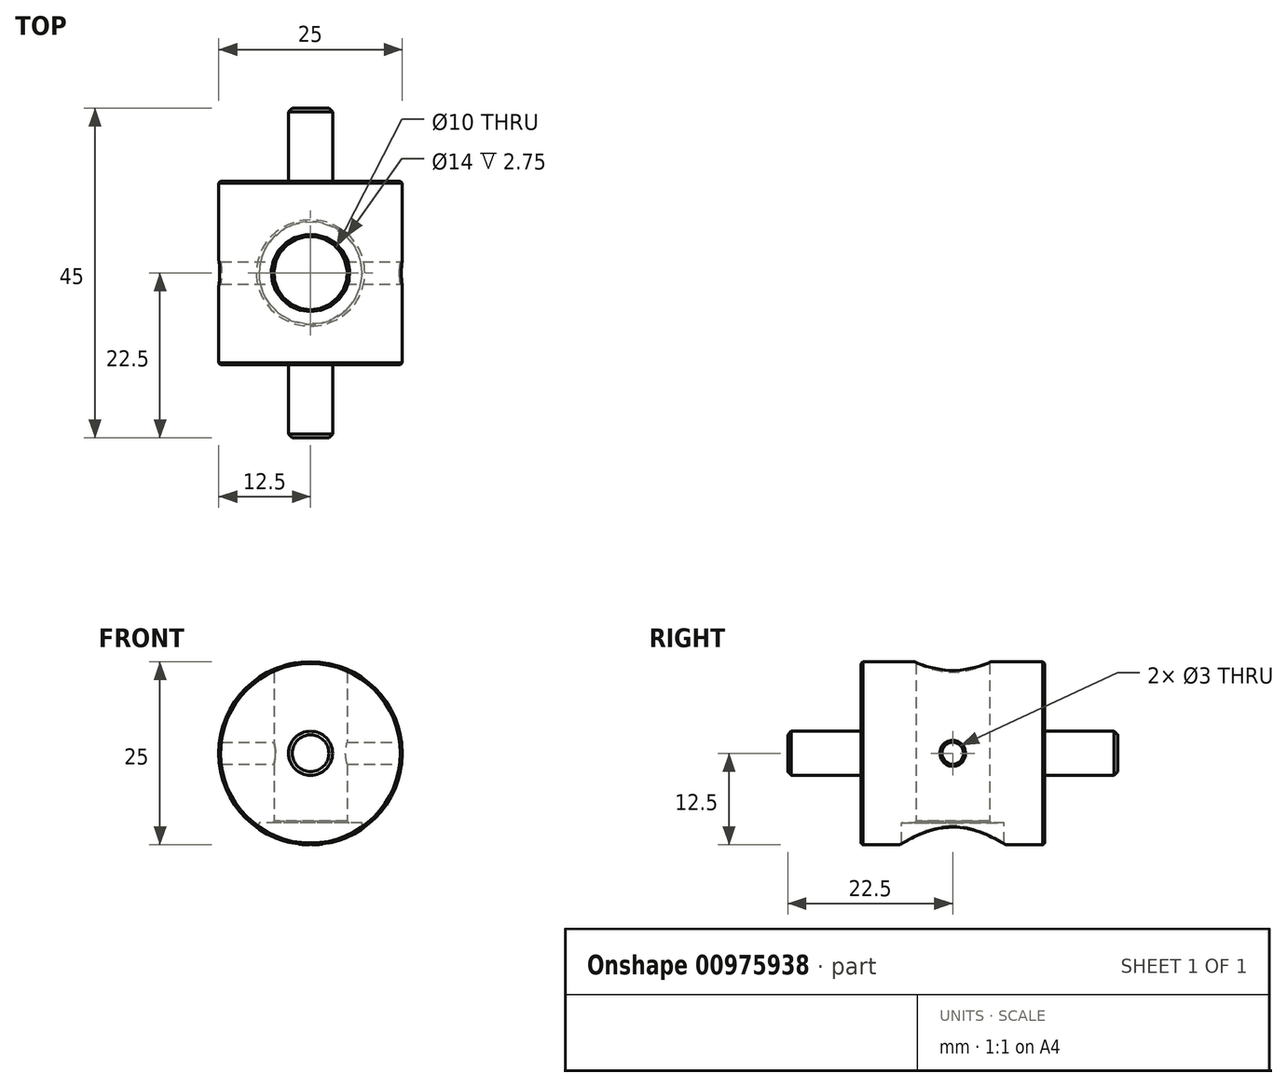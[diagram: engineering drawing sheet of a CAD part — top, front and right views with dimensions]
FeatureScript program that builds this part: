
annotation { "Feature Type Name" : "Feature", "Feature Type Description" : "" }
export const myFeature = defineFeature(function(context is Context, id is Id, definition is map)
    precondition{}
    {
        {
            var Q0;
            Q0=qCreatedBy(makeId("Front.planeOp"),FACE);
            var sketch = newSketch(context, id + "F0", { "sketchPlane" : qUnion([Q0])});
            skCircle(sketch, "E0", {"center": v(0, 0) * mm, "radius": 12.5 * mm});
            skSolve(sketch);
        }
        {
            var Q0;
            Q0=makeQuery(id+"F0.imprint","IMPRINT",FACE,{"disambiguationData":[TD([[makeQuery(id+"F0.imprint","IMPRINT",EDGE,{"derivedFrom":sQuery(id+"F0.wireOp",EDGE,"E0")}),1.0]])]});
            extrude(context, id + "F1", {"entities" : qUnion([Q0]), "depth" : 25 * mm, "offsetDistance" : 25 * mm, "symmetric" : true});
        }
        {
            var Q0;
            Q0=makeQuery(id+"F1.opExtrude","CAP_FACE",FACE,{"disambiguationData":[OSD([sQuery(id+"F0.wireOp",EDGE,"E0")])],"isStart":false});
            var sketch = newSketch(context, id + "F2", { "sketchPlane" : qUnion([Q0])});
            skCircle(sketch, "E1", {"center": v(0, 0) * mm, "radius": 3 * mm});
            skSolve(sketch);
        }
        {
            var Q0;
            Q0=makeQuery(id+"F2.imprint","IMPRINT",FACE,{"disambiguationData":[TD([[makeQuery(id+"F2.imprint","IMPRINT",EDGE,{"derivedFrom":sQuery(id+"F2.wireOp",EDGE,"E1")}),1.0]])]});
            extrude(context, id + "F3", {"entities" : qUnion([Q0]), "operationType" : NewBodyOperationType.ADD, "depth" : 10 * mm, "offsetDistance" : 25 * mm});
        }
        {
            var Q0;
            Q0=makeQuery(id+"F1.opExtrude","CAP_FACE",FACE,{"disambiguationData":[OSD([sQuery(id+"F0.wireOp",EDGE,"E0")])],"isStart":true});
            var sketch = newSketch(context, id + "F4", { "sketchPlane" : qUnion([Q0])});
            skCircle(sketch, "E2", {"center": v(0, 0) * mm, "radius": 3 * mm});
            skSolve(sketch);
        }
        {
            var Q0;
            Q0=makeQuery(id+"F4.imprint","IMPRINT",FACE,{"disambiguationData":[TD([[makeQuery(id+"F4.imprint","IMPRINT",EDGE,{"derivedFrom":sQuery(id+"F4.wireOp",EDGE,"E2")}),1.0]])]});
            extrude(context, id + "F5", {"entities" : qUnion([Q0]), "operationType" : NewBodyOperationType.ADD, "depth" : 10 * mm, "offsetDistance" : 25 * mm});
        }
        {
            var Q0;
            Q0=makeQuery(id+"F5.opExtrude","CAP_EDGE",EDGE,{"disambiguationData":[OSD([sQuery(id+"F4.wireOp",EDGE,"E2")])],"isStart":false});
            var Q1;
            Q1=makeQuery(id+"F3.opExtrude","CAP_EDGE",EDGE,{"disambiguationData":[OSD([sQuery(id+"F2.wireOp",EDGE,"E1")])],"isStart":false});
            chamfer(context, id + "F6", {"entities" : qUnion([Q0, Q1]), "width" : 0.5 * mm, "tangentPropagation" : true});
        }
        {
            var Q0;
            Q0=makeQuery(id+"F1.opExtrude","CAP_EDGE",EDGE,{"disambiguationData":[OSD([sQuery(id+"F0.wireOp",EDGE,"E0")])],"isStart":true});
            var Q1;
            Q1=makeQuery(id+"F1.opExtrude","CAP_EDGE",EDGE,{"disambiguationData":[OSD([sQuery(id+"F0.wireOp",EDGE,"E0")])],"isStart":false});
            chamfer(context, id + "F7", {"entities" : qUnion([Q0, Q1]), "width" : 0.25 * mm, "tangentPropagation" : true});
        }
        {
            var Q0;
            Q0=qCreatedBy(makeId("Top.planeOp"),FACE);
            var sketch = newSketch(context, id + "F8", { "sketchPlane" : qUnion([Q0])});
            skCircle(sketch, "E3", {"center": v(0, 0) * mm, "radius": 5 * mm});
            skSolve(sketch);
        }
        {
            var Q0;
            Q0 = qSketchRegion(id + "F8", true);
            extrude(context, id + "F9", {"entities" : qUnion([Q0]), "operationType" : NewBodyOperationType.REMOVE, "depth" : 25 * mm, "offsetDistance" : 25 * mm, "symmetric" : true});
        }
        {
            var Q0;
            Q0=qCreatedBy(makeId("Top.planeOp"),FACE);
            var sketch = newSketch(context, id + "F10", { "sketchPlane" : qUnion([Q0])});
            skCircle(sketch, "E4", {"center": v(0, 0) * mm, "radius": 7 * mm});
            skSolve(sketch);
        }
        {
            var Q0;
            Q0 = qSketchRegion(id + "F10", true);
            extrude(context, id + "F11", {"entities" : qUnion([Q0]), "operationType" : NewBodyOperationType.REMOVE, "oppositeDirection" : true, "depth" : 25 * mm, "offsetDistance" : 25 * mm, "hasSecondDirection" : true, "secondDirectionOppositeDirection" : true, "secondDirectionDepth" : 9.5 * mm});
        }
        {
            var Q0;
            Q0=qCreatedBy(makeId("Right.planeOp"),FACE);
            var sketch = newSketch(context, id + "F12", { "sketchPlane" : qUnion([Q0])});
            skCircle(sketch, "E5", {"center": v(0, 0) * mm, "radius": 1.5 * mm});
            skSolve(sketch);
        }
        {
            var Q0;
            Q0 = qSketchRegion(id + "F12", true);
            extrude(context, id + "F13", {"entities" : qUnion([Q0]), "operationType" : NewBodyOperationType.REMOVE, "oppositeDirection" : true, "depth" : 25 * mm, "offsetDistance" : 25 * mm, "symmetric" : true});
        }
        {
            var Q0;
            Q0=makeQuery(id+"F13.boolean.opBoolean","INTERSECT",EDGE,{"disambiguationData":[OD(1.0)],"derivedFrom":[makeQuery(id+"F1.opExtrude","SWEPT_FACE",FACE,{"disambiguationData":[OSD([sQuery(id+"F0.wireOp",EDGE,"E0")])]}),makeQuery(id+"F13.opExtrude","SWEPT_FACE",FACE,{"disambiguationData":[OSD([sQuery(id+"F12.wireOp",EDGE,"E5")])]})]});
            var Q1;
            Q1=makeQuery(id+"F11.boolean.opBoolean","INTERSECT",EDGE,{"derivedFrom":[makeQuery(id+"F1.opExtrude","SWEPT_FACE",FACE,{"disambiguationData":[OSD([sQuery(id+"F0.wireOp",EDGE,"E0")])]}),makeQuery(id+"F11.opExtrude","SWEPT_FACE",FACE,{"disambiguationData":[OSD([sQuery(id+"F10.wireOp",EDGE,"E4")])]})]});
            var Q2;
            Q2=makeQuery(id+"F9.boolean.opBoolean","INTERSECT",EDGE,{"disambiguationData":[OD(1.0)],"derivedFrom":[makeQuery(id+"F1.opExtrude","SWEPT_FACE",FACE,{"disambiguationData":[OSD([sQuery(id+"F0.wireOp",EDGE,"E0")])]}),makeQuery(id+"F9.opExtrude","SWEPT_FACE",FACE,{"disambiguationData":[OSD([sQuery(id+"F8.wireOp",EDGE,"E3")])]})]});
            var Q3;
            Q3=makeQuery(id+"F13.boolean.opBoolean","INTERSECT",EDGE,{"disambiguationData":[OD(0.0)],"derivedFrom":[makeQuery(id+"F1.opExtrude","SWEPT_FACE",FACE,{"disambiguationData":[OSD([sQuery(id+"F0.wireOp",EDGE,"E0")])]}),makeQuery(id+"F13.opExtrude","SWEPT_FACE",FACE,{"disambiguationData":[OSD([sQuery(id+"F12.wireOp",EDGE,"E5")])]})]});
            var Q4;
            Q4=makeQuery(id+"F11.boolean.opBoolean","INTERSECT",EDGE,{"derivedFrom":[makeQuery(id+"F9.boolean.opBoolean","COPY",FACE,{"derivedFrom":makeQuery(id+"F9.opExtrude","SWEPT_FACE",FACE,{"disambiguationData":[OSD([sQuery(id+"F8.wireOp",EDGE,"E3")])]})}),makeQuery(id+"F11.opExtrude","CAP_FACE",FACE,{"disambiguationData":[OSD([sQuery(id+"F10.wireOp",EDGE,"E4")])],"isStart":true})]});
            chamfer(context, id + "F14", {"entities" : qUnion([Q0, Q1, Q2, Q3, Q4]), "width" : 0.25 * mm, "tangentPropagation" : true});
        }
    });
